# Revit family: FRC_BICCHIERI
name_source: partatom
category: Generic Models
revit_build: Autodesk Revit 2013 (Build: 20120221_2030(x64)
units: mm (PartAtom-declared; Revit-internal decimal feet)

## types (4) — shared parameters
Default Elevation = 121.92 cm

## per-type parameters (varying)
| type | Altezza totale | Area | Raggio inf bicchiere | Raggio sup bicchiere | Volume | altezza base | diametro base | diametro inferiore bicchiere | diametro sup bicchiere | raggio base | raggio inf cavità | raggio sup cavità |
| TUMBLER BASSO | 8.7 cm | 38.47 cm² | 3.65 cm | 3.65 cm | 0.28 L | 1.45 cm | 7.3 cm | 7.3 cm | 7.3 cm | 3.65 cm | 3.5 cm | 3.5 cm |
| TUMBLER ALTO | 16.5 cm | 23.75 cm² | 2.9 cm | 2.9 cm | 0.33 L | 2.75 cm | 5.8 cm | 5.8 cm | 5.8 cm | 2.9 cm | 2.75 cm | 2.75 cm |
| OLD FASHIONED | 8.7 cm | 38.47 cm² | 3.65 cm | 4.5 cm | 0.28 L | 1.45 cm | 7.3 cm | 7.3 cm | 9 cm | 3.65 cm | 3.5 cm | 4.35 cm |
| APERITIVO | 14.8 cm | 17.34 cm² | 2.5 cm | 3.5 cm | 0.21 L | 2.47 cm | 7 cm | 5 cm | 7 cm | 3.5 cm | 2.35 cm | 3.35 cm |

## geometry (parser evidence)
native form markers: Sweep x1
no freeform markers — native parametric forms only
